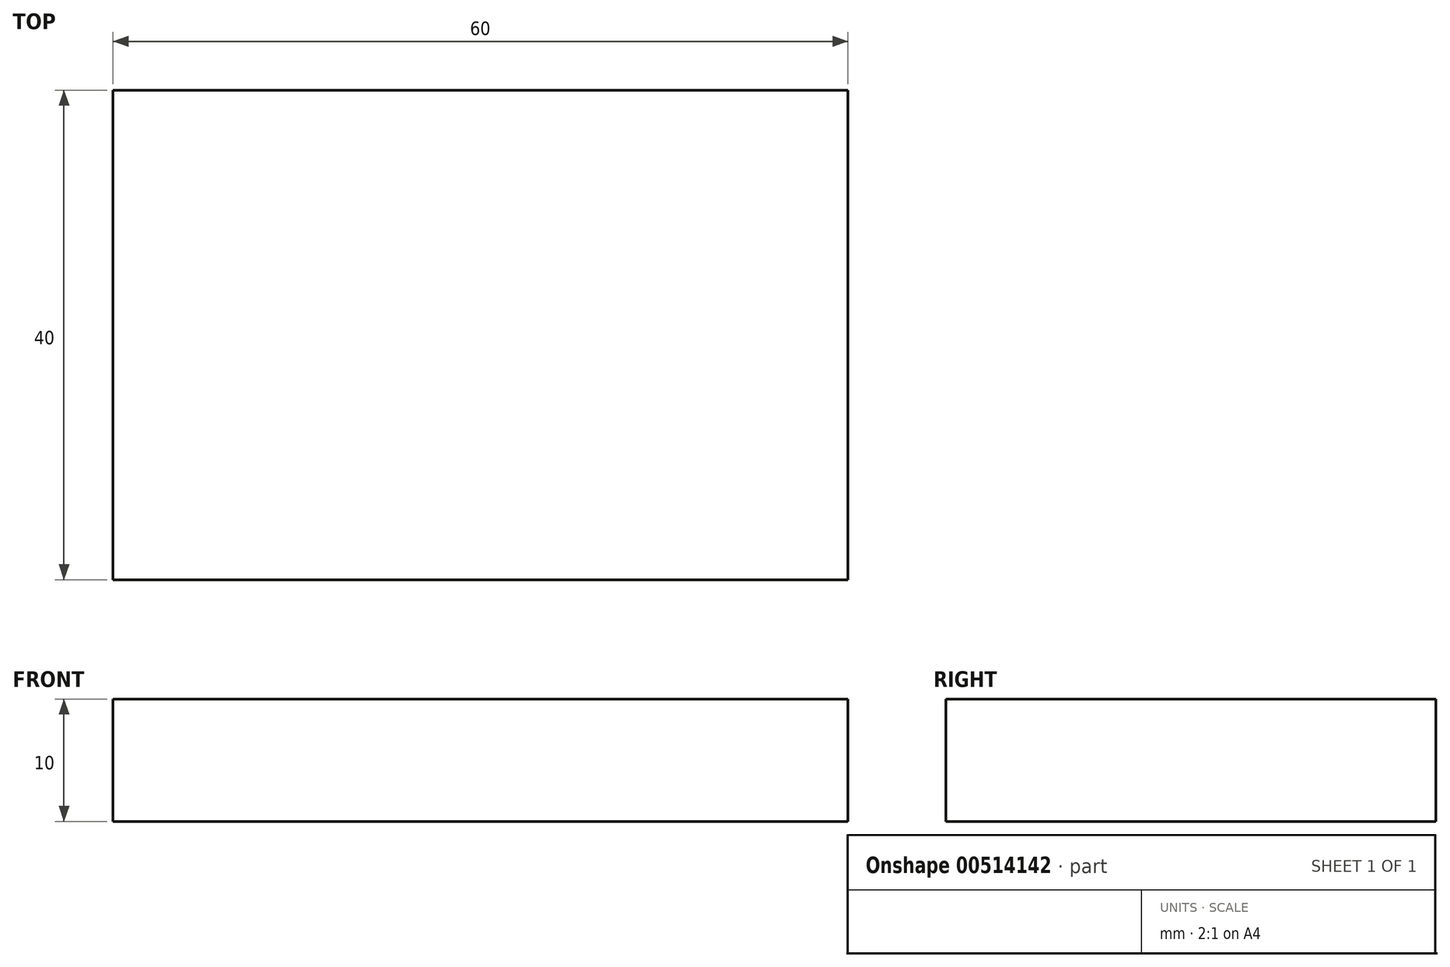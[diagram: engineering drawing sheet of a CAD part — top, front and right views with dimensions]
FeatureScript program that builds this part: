
annotation { "Feature Type Name" : "Feature", "Feature Type Description" : "" }
export const myFeature = defineFeature(function(context is Context, id is Id, definition is map)
    precondition{}
    {
        {
            var Q0;
            Q0=qCreatedBy(makeId("Top.planeOp"),FACE);
            var sketch = newSketch(context, id + "F0", { "sketchPlane" : qUnion([Q0])});
            skLineSegment(sketch, "E0.bottom", {"start": v(0, 0) * mm, "end": v(60, 0) * mm});
            skLineSegment(sketch, "E0.top", {"start": v(0, 40) * mm, "end": v(60, 40) * mm});
            skLineSegment(sketch, "E0.left", {"start": v(0, 0) * mm, "end": v(0, 40) * mm});
            skLineSegment(sketch, "E0.right", {"start": v(60, 0) * mm, "end": v(60, 40) * mm});
            skSolve(sketch);
        }
        {
            var Q0;
            Q0 = qSketchRegion(id + "F0", true);
            extrude(context, id + "F1", {"entities" : qUnion([Q0]), "depth" : 10 * mm});
        }
    });
